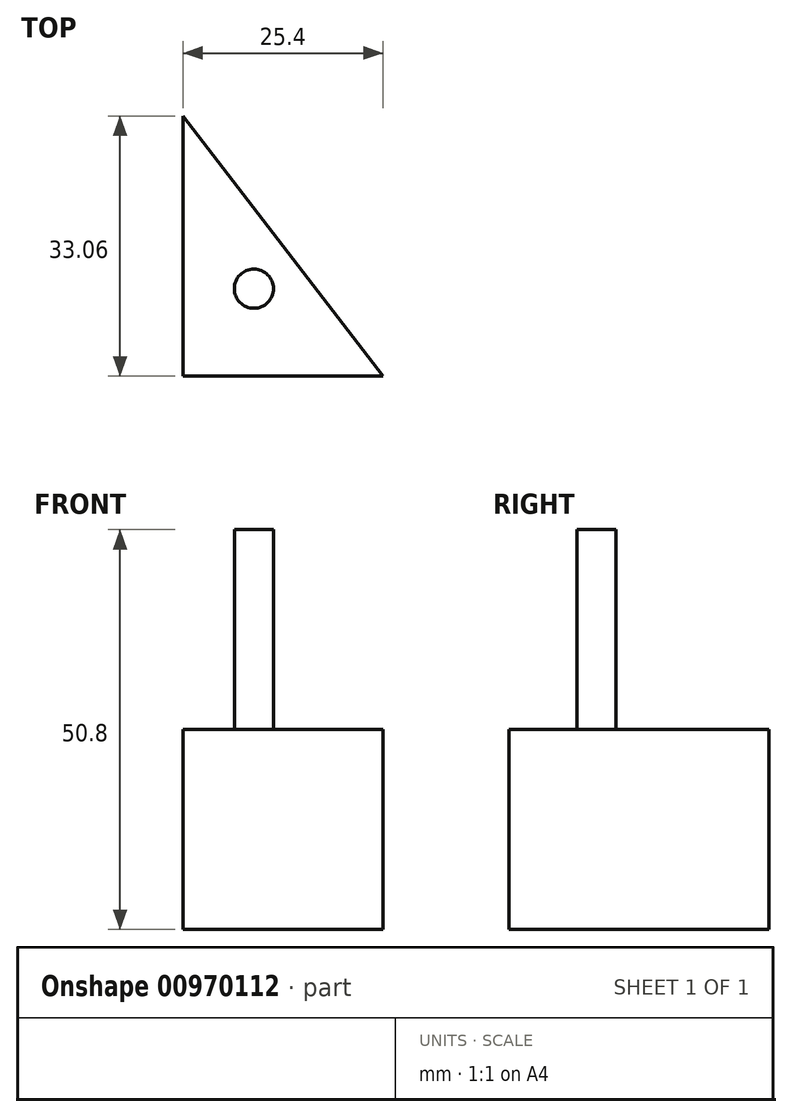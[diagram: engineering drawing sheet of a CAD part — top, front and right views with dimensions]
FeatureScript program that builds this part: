
annotation { "Feature Type Name" : "Feature", "Feature Type Description" : "" }
export const myFeature = defineFeature(function(context is Context, id is Id, definition is map)
    precondition{}
    {
        {
            var Q0;
            Q0=qCreatedBy(makeId("Top.planeOp"),FACE);
            var sketch = newSketch(context, id + "F0", { "sketchPlane" : qUnion([Q0])});
            skLineSegment(sketch, "E0", {"start": v(0, 0) * mm, "end": v(-25.4, 0) * mm});
            skLineSegment(sketch, "E1", {"start": v(-25.4, 0) * mm, "end": v(-25.4, 33.06) * mm});
            skLineSegment(sketch, "E2", {"start": v(-25.4, 33.06) * mm, "end": v(0, 0) * mm});
            skSolve(sketch);
        }
        {
            var Q0;
            Q0=makeQuery(id+"F0.imprint","IMPRINT",FACE,{"disambiguationData":[TD([[makeQuery(id+"F0.imprint","IMPRINT",EDGE,{"derivedFrom":sQuery(id+"F0.wireOp",EDGE,"E0")}),-1.0]])]});
            extrude(context, id + "F1", {"entities" : qUnion([Q0]), "depth" : 25.4 * mm, "offsetDistance" : 25.4 * mm});
        }
        {
            var Q0;
            Q0=makeQuery(id+"F1.opExtrude","CAP_FACE",FACE,{"disambiguationData":[OSD([sQuery(id+"F0.wireOp",EDGE,"E0"),sQuery(id+"F0.wireOp",EDGE,"E1"),sQuery(id+"F0.wireOp",EDGE,"E2")])],"isStart":false});
            var sketch = newSketch(context, id + "F2", { "sketchPlane" : qUnion([Q0])});
            skCircle(sketch, "E3", {"center": v(-16.4, 11.12) * mm, "radius": 2.49 * mm});
            skSolve(sketch);
        }
        {
            var Q0;
            Q0=makeQuery(id+"F2.imprint","IMPRINT",FACE,{"disambiguationData":[TD([[makeQuery(id+"F2.imprint","IMPRINT",EDGE,{"derivedFrom":sQuery(id+"F2.wireOp",EDGE,"E3")}),1.0]])]});
            extrude(context, id + "F3", {"entities" : qUnion([Q0]), "operationType" : NewBodyOperationType.ADD, "depth" : 25.4 * mm, "offsetDistance" : 25.4 * mm});
        }
    });
